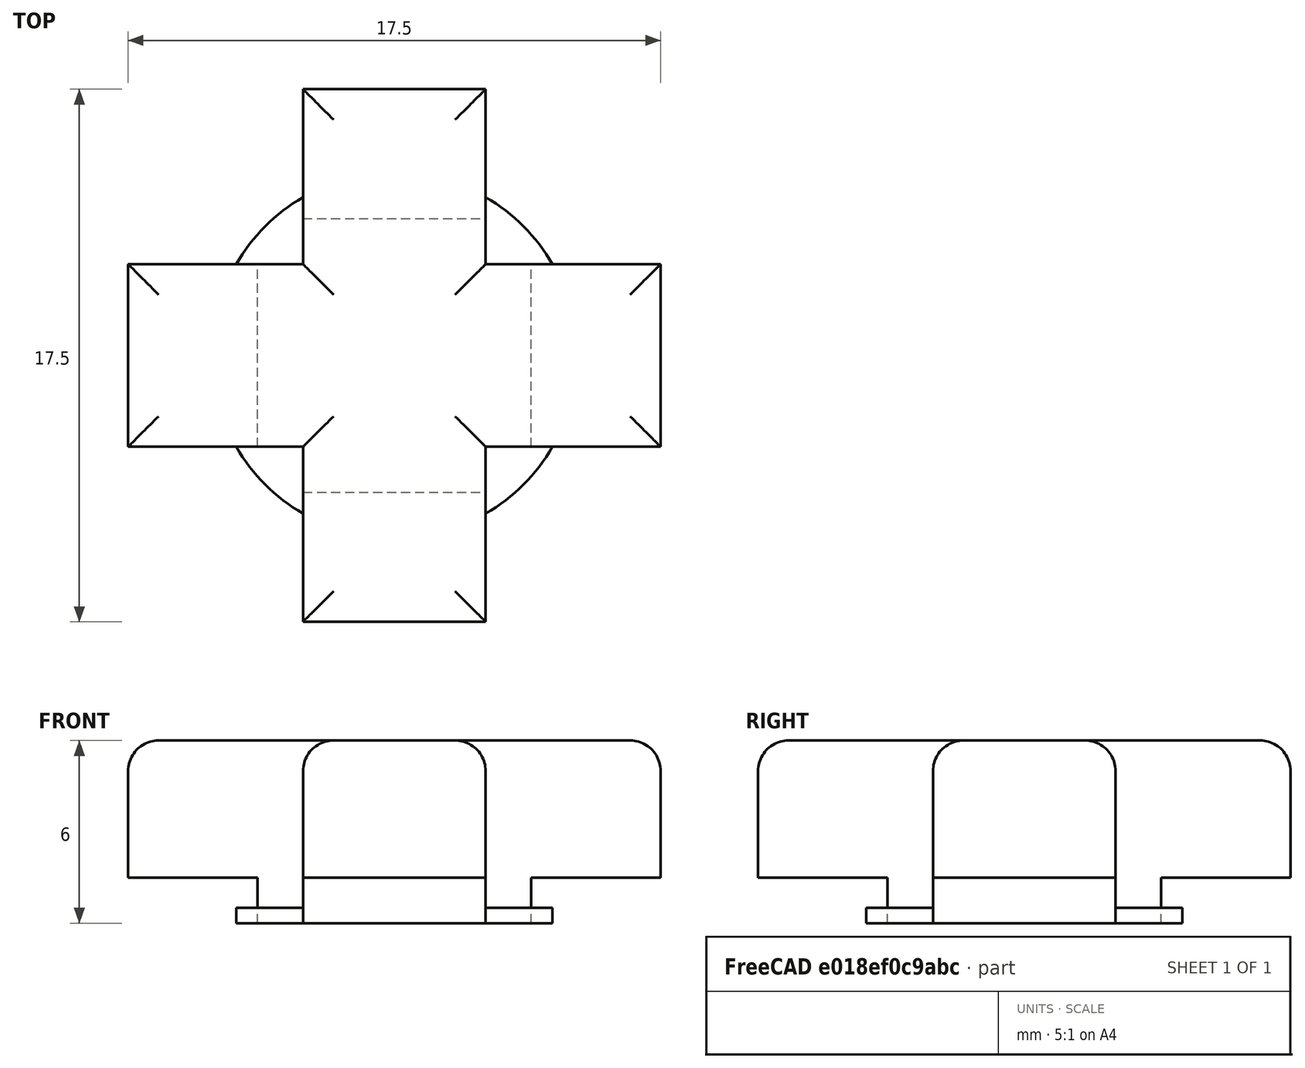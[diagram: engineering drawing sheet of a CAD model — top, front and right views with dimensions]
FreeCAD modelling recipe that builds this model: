
FCSTD DOCUMENT  (FreeCAD 0.18R16131 (Git))
Label: GBC_d_pad_new
License: All rights reserved
LicenseURL: http://en.wikipedia.org/wiki/All_rights_reserved
objects: Part::Box×6, Part::Cut×4, Part::Fillet×2, Part::MultiFuse×2, Part::Cylinder×1
note: 15 computed .brp shape members not serialized (recipe doc carries the construction recipe); baked Part::Feature solids carry a one-line shape summary decoded from their .brp

FEATURE [Part::Cylinder] Cylinder
  Angle = 360
  AttacherType = Attacher::AttachEngine3D
  Height = 0.5
  Radius = 6
FEATURE [Part::Box] Box006  label="Cube(dpad_horizontal_full)"
  AttacherType = Attacher::AttachEngine3D
  Height = 6
  Length = 17.5
  Placement = pos=(-8.75,-3,0) rot=(0,0,1;0rad)
  Width = 6
FEATURE [Part::Box] Box007  label="Cube(dpad_vertical_full)"
  AttacherType = Attacher::AttachEngine3D
  Height = 6
  Length = 6
  Placement = pos=(-3,-8.75,0) rot=(0,0,1;0rad)
  Width = 17.5
FEATURE [Part::Fillet] Fillet
  Base = -> Box007
  Edges = 4 edges r=1: [Edge2,Edge6,Edge10,Edge12]
FEATURE [Part::Fillet] Fillet001
  Base = -> Box006
  Edges = 4 edges r=1: [Edge2,Edge6,Edge10,Edge12]
FEATURE [Part::MultiFuse] Fusion
  Shapes = -> [Fillet001,Fillet]
FEATURE [Part::Box] Box008  label="Cube"
  AttacherType = Attacher::AttachEngine3D
  Height = 1.5
  Length = 10
  Placement = pos=(4.5,-3,0) rot=(0,0,1;0rad)
  Width = 6
FEATURE [Part::Box] Box009  label="Cube001"
  AttacherType = Attacher::AttachEngine3D
  Height = 1.5
  Length = 10
  Placement = pos=(-14.5,-3,0) rot=(0,0,1;0rad)
  Width = 6
FEATURE [Part::Box] Box010  label="Cube002"
  AttacherType = Attacher::AttachEngine3D
  Height = 1.5
  Length = 6
  Placement = pos=(-3,4.5,0) rot=(0,0,1;0rad)
  Width = 10
FEATURE [Part::Box] Box011  label="Cube003"
  AttacherType = Attacher::AttachEngine3D
  Height = 1.5
  Length = 6
  Placement = pos=(-3,-14.5,0) rot=(0,0,1;0rad)
  Width = 10
FEATURE [Part::MultiFuse] Fusion001
  Shapes = -> [Cylinder,Fusion]
FEATURE [Part::Cut] Cut
  Base = -> Fusion001
  Tool = -> Box011
FEATURE [Part::Cut] Cut001
  Base = -> Cut
  Tool = -> Box010
FEATURE [Part::Cut] Cut002
  Base = -> Cut001
  Tool = -> Box009
FEATURE [Part::Cut] Cut003
  Base = -> Cut002
  Tool = -> Box008
